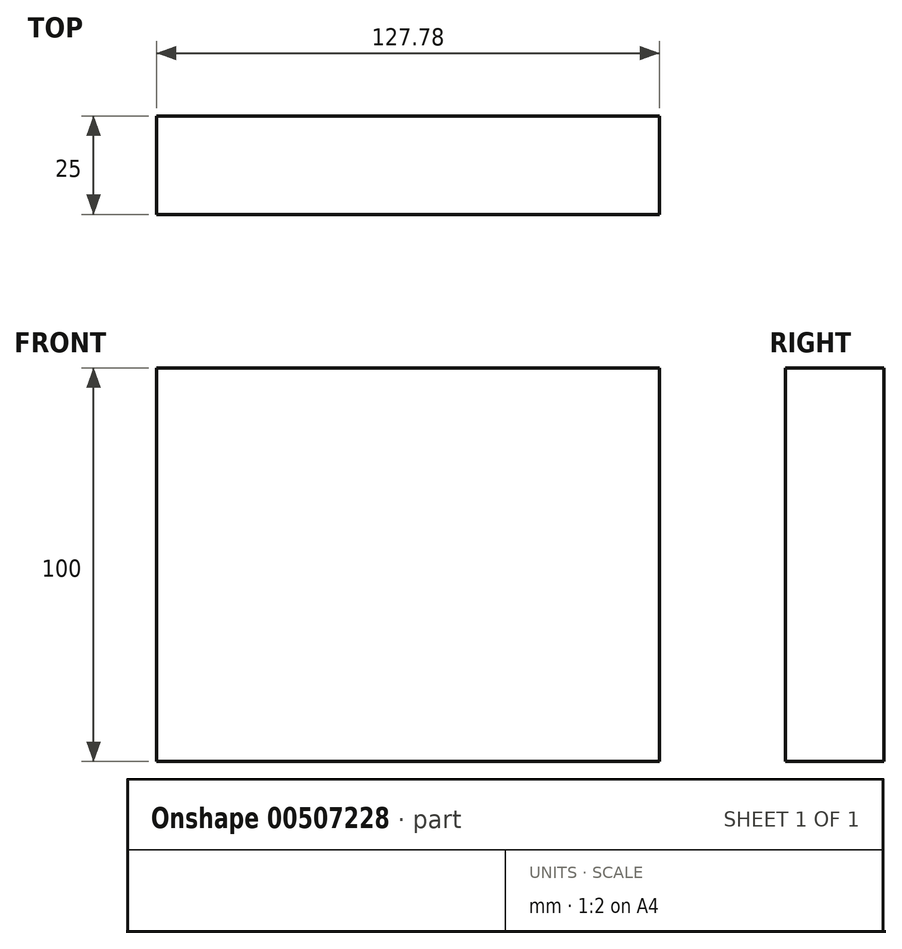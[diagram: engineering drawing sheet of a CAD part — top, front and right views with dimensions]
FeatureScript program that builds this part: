
annotation { "Feature Type Name" : "Feature", "Feature Type Description" : "" }
export const myFeature = defineFeature(function(context is Context, id is Id, definition is map)
    precondition{}
    {
        {
            var Q0;
            Q0=qCreatedBy(makeId("Front.planeOp"),FACE);
            var sketch = newSketch(context, id + "F0", { "sketchPlane" : qUnion([Q0])});
            skLineSegment(sketch, "E0.bottom", {"start": v(63.9, -50) * mm, "end": v(-63.9, -50) * mm});
            skLineSegment(sketch, "E0.top", {"start": v(63.9, 50) * mm, "end": v(-63.9, 50) * mm});
            skLineSegment(sketch, "E0.left", {"start": v(63.9, -50) * mm, "end": v(63.9, 50) * mm});
            skLineSegment(sketch, "E0.right", {"start": v(-63.9, -50) * mm, "end": v(-63.9, 50) * mm});
            skPoint(sketch, "E0.middle", {"position": v(0, 0) * mm});
            skSolve(sketch);
        }
        {
            var Q0;
            Q0=makeQuery(id+"F0.imprint","IMPRINT",FACE,{"disambiguationData":[TD([[makeQuery(id+"F0.imprint","IMPRINT",EDGE,{"derivedFrom":sQuery(id+"F0.wireOp",EDGE,"E0.bottom")}),-1.0]])]});
            extrude(context, id + "F1", {"entities" : qUnion([Q0]), "depth" : 25 * mm, "offsetDistance" : 25 * mm});
        }
    });
